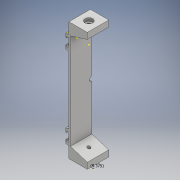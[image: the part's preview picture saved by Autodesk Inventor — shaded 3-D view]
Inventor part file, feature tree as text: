
AUTODESK INVENTOR PART (.ipt)
format: ipt  version: 2018 (Build 220112000, 112)  size: 768,512 bytes
history: native  units: mm
features: sketch x39, extrude x28, fillet x4, chamfer x2
ambient origin geometry x8: Origin, YZ Plane, XZ Plane, XY Plane, X Axis, Y Axis, Z Axis, Center Point
bodies: Solid1 (feature_tree)
feature tree (73):
  extrude  "Extrusion1"  Depth=125.0mm
  extrude  "Extrusion2"  Depth=2.0mm
  extrude  "Extrusion3"  Depth=2.0mm TaperAngle=0.0deg
  extrude  "Extrusion4"  Depth=7.1mm TaperAngle=0.0deg
  extrude  "Extrusion5"  Depth=155.0mm TaperAngle=0.0deg
  chamfer  "Chamfer1"  Distance=7.1mm
  sketch  "Sketch6"  dims[d16=22.0mm d17=7.1mm d18=0.0mm d19=7.0mm d20=2.0mm d21=12.61873mm]
  chamfer  "Chamfer2"  Distance=2.0mm
  sketch  "Sketch7"  dims[d22=7.0mm d23=2.0mm d24=12.61873mm d25=8.0mm]
  sketch  "Sketch8"  dims[d26=2.0mm d27=0.0mm d28=8.0mm]
  sketch  "Sketch9"  dims[d29=2.0mm d30=0.0mm d31=2.0mm d32=0.0mm]
  extrude  "Extrusion6"  Depth=2.0mm
  extrude  "Extrusion7"  Depth=2.0mm
  extrude  "Extrusion8"  Depth=2.0mm TaperAngle=0.0deg
  extrude  "Extrusion9"  Depth=2.0mm
  sketch  "Sketch13"  dims[d45=2.0mm d46=38.0mm]
  sketch  "Sketch14"  dims[d47=2.0mm d48=0.0mm d49=38.0mm]
  extrude  "Extrusion10"  Depth=2.0mm
  sketch  "Sketch16"  dims[d53=38.0mm d54=40.75mm]
  extrude  "Extrusion11"  Depth=2.0mm TaperAngle=0.0deg
  fillet  "Fillet1"  Radius=2.0mm
  fillet  "Fillet2"  Radius=2.0mm
  extrude  "Extrusion12"  Depth=2.0mm
  extrude  "Extrusion13"  Depth=2.0mm
  extrude  "Extrusion14"  Depth=21.75mm
  sketch  "Sketch21"  dims[d67=12.0mm d68=3.0mm]
  extrude  "Extrusion15"  Depth=40.75mm
  extrude  "Extrusion16"  Depth=40.75mm
  sketch  "Sketch24"  dims[d75=5.0mm d76=5.0mm]
  sketch  "Sketch25"  dims[d77=5.0mm d78=5.0mm]
  extrude  "Extrusion17"  Depth=32.0mm TaperAngle=0.0deg
  extrude  "Extrusion18"  Depth=12.0mm
  sketch  "Sketch28"  dims[d85=30.0mm d86=0.0mm d87=30.0mm d88=0.0mm]
  fillet  "Fillet3"  Radius=3.0mm
  extrude  "Extrusion19"  Depth=3.0mm
  extrude  "Extrusion20"  Depth=3.0mm
  sketch  "Sketch31"  dims[d96=10.0mm]
  extrude  "Extrusion21"  Depth=2.0mm
  extrude  "Extrusion22"  Depth=2.0mm TaperAngle=0.0deg
  extrude  "Extrusion23"  Depth=5.0mm
  extrude  "Extrusion24"  Depth=5.0mm
  extrude  "Extrusion25"  Depth=9.375mm
  extrude  "Extrusion26"  Depth=2.0mm TaperAngle=0.0deg
  extrude  "Extrusion27"  Depth=30.0mm TaperAngle=0.0deg
  extrude  "Extrusion28"  Depth=28.0mm TaperAngle=0.0deg
  fillet  "Fillet4"  Radius=4.0mm
  sketch  "Sketch1"  dims[d0=24.0mm d1=125.0mm]
  sketch  "Sketch2"  dims[d2=2.0mm d3=0.0mm d4=15.0mm]
  sketch  "Sketch3"  dims[d5=15.0mm d6=22.0mm d7=2.0mm d8=0.0mm d9=0.0mm]
  sketch  "Sketch4"  dims[d10=22.0mm d11=7.1mm d12=0.0mm]
  sketch  "Sketch5"  dims[d13=9.0mm d14=155.0mm d15=0.0mm]
  sketch  "Sketch10"  dims[d33=2.0mm d34=0.0mm d35=5.5mm]
  sketch  "Sketch11"  dims[d36=11.0mm d37=2.0mm]
  sketch  "Sketch12"  dims[d38=2.0mm d39=7.0mm d40=0.0mm d42=2.0mm d43=0.0mm d44=2.0mm]
  sketch  "Sketch15"  dims[d51=43.5mm d52=21.75mm]
  sketch  "Sketch17"  dims[d55=38.0mm d56=40.75mm]
  sketch  "Sketch18"  dims[d57=30.0mm d58=0.0mm d59=32.0mm d60=0.0mm]
  sketch  "Sketch19"  dims[d61=3.0mm d62=12.0mm d63=3.0mm]
  sketch  "Sketch20"  dims[d64=3.1mm d65=0.0mm d66=3.0mm]
  sketch  "Sketch22"  dims[d69=3.1mm d70=0.0mm d71=2.0mm]
  sketch  "Sketch23"  dims[d72=2.0mm d73=3.6mm d74=0.0mm]
  sketch  "Sketch26"  dims[d79=1.0mm d80=0.0mm d81=9.375mm]
  sketch  "Sketch27"  dims[d82=2.0mm d83=100.0mm d84=0.0mm]
  sketch  "Sketch29"  dims[d89=8.0mm d90=0.0mm d91=28.0mm d92=0.0mm d93=4.0mm]
  sketch  "Sketch30"  dims[d94=169.0mm d95=0.0mm]
  sketch  "Sketch32"  dims[d97=4.0mm d98=0.0mm]
  sketch  "Sketch33"  dims[d99=4.0mm d100=0.0mm]
  sketch  "Sketch34"  dims[d101=6.35mm]
  sketch  "Sketch35"  dims[d102=40.0mm d103=0.0mm]
  sketch  "Sketch36"  dims[d104=1.0mm]
  sketch  "Sketch37"  dims[d105=1.0mm]
  sketch  "Sketch38"  dims[d106=5.0mm d107=0.0mm]
  sketch  "Sketch39"  dims[d108=2.0mm]
